# Revit family: Faucet-Single_Handle-Grohe-Eurosmart_Cosmopolitan-3287500A
name_source: partatom
category: Plumbing Fixtures
revit_build: Autodesk Revit 2018 (Build: 20170223_1515(x64)
units: mm (PartAtom-declared; Revit-internal decimal feet)

## family parameters
Always vertical = No
Cut with Voids When Loaded = No
OmniClass Number = 23.45.55.14
OmniClass Title = Single Faucets
Part Type = Normal
Room Calculation Point = No
Round Connector Dimension = Use Diameter
Shared = Yes
Work Plane-Based = Yes

## types (1)
- 3287500A
    ADA Compliant = Yes
    Assembly Code = D2020300
    CW Connection = No
    CWFU = 1.5
    Default Elevation = 0"
    Description = Eurosmart Cosmopolitan Single-Handle S-Size Bathroom Faucet
    Finish = Brass-Grohe-00A-Starlight Chrome
    Flow Rate = 1.2 gpm (4.56 L/min)
    HW Connection = No
    HWFU = 1.5
    Height = 5 13/16"
    IAPMO Compliance = Energy Policy Act of 1992, NSF 61, ASME A112.18.1/CSA B125.1, US Federal and State material regulations,  EPA WaterSense® and ICC/ANSI A117.1
    Installation Type = Deck-Mounted
    Length = 6"
    Manufacturer = Grohe
    Material = Brass-Grohe-00A-Starlight Chrome
    Model = 3287500A
    Price = Prices may vary. Please consult Manufacturer Representative for most up-to-date price list.
    Product Documentation Link = https://americanstandard.box.com
    Product Page URL = https://www.grohe.us
    Revised Date = 12/07/2021
    Tempered Water Connection = Yes
    Tempered Water Connection Diameter = 3/8"
    Type Comments = Single hole installation with SilkMove 1.4inch (35 mm) ceramic cartridge that delivers a lifetime of ultra-smooth operation and precise control of the water temperature and volume; 1 1/4 inch pop-up waste set, StarLight chrome finish for flawless, robust, long-lasting designed to be extremely resistant to dirt and scratches, adjustable flow rate limiter; stainless steel flex lines; QuickFix installation system with centering support to reduce installation time by as much as 50 percent and save money; GROHE EcoJoy — reduces water consumption by up to 50 percent; single lever handle; and nylon reinforced braided flexible inlet hoses.
    URL = https://www.grohe.us
    Vent Connection = No
    WFU = 2
    Waste Connection = No
    Waste Set = 1 1/4 inch Pop-up Waste Set

## geometry (parser evidence)
native form markers: Sweep x2
no freeform markers — native parametric forms only
